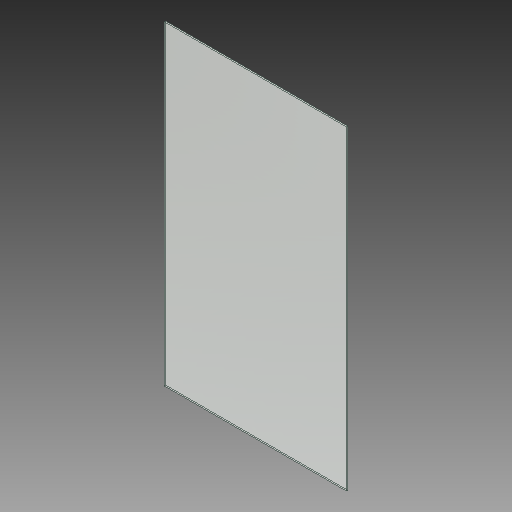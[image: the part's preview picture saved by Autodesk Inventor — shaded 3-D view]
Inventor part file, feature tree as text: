
AUTODESK INVENTOR PART (.ipt)
format: ipt  version: 2017 (Build 210142000, 142)  size: 91,648 bytes
history: native  units: in
note: dims shown in document units (in); Inventor stores cm internally (conversion verified against a paired STEP export)
features: extrude x1, sketch x1
ambient origin geometry x8: Origin, YZ Plane, XZ Plane, XY Plane, X Axis, Y Axis, Z Axis, Center Point
bodies: Solid1 (feature_tree)
feature tree (2):
  extrude  "Extrusion1"  Depth=16.875in
  sketch  "Sketch1"  dims[d0=29.25in d1=16.875in d2=0.125in d3=0.0in]
